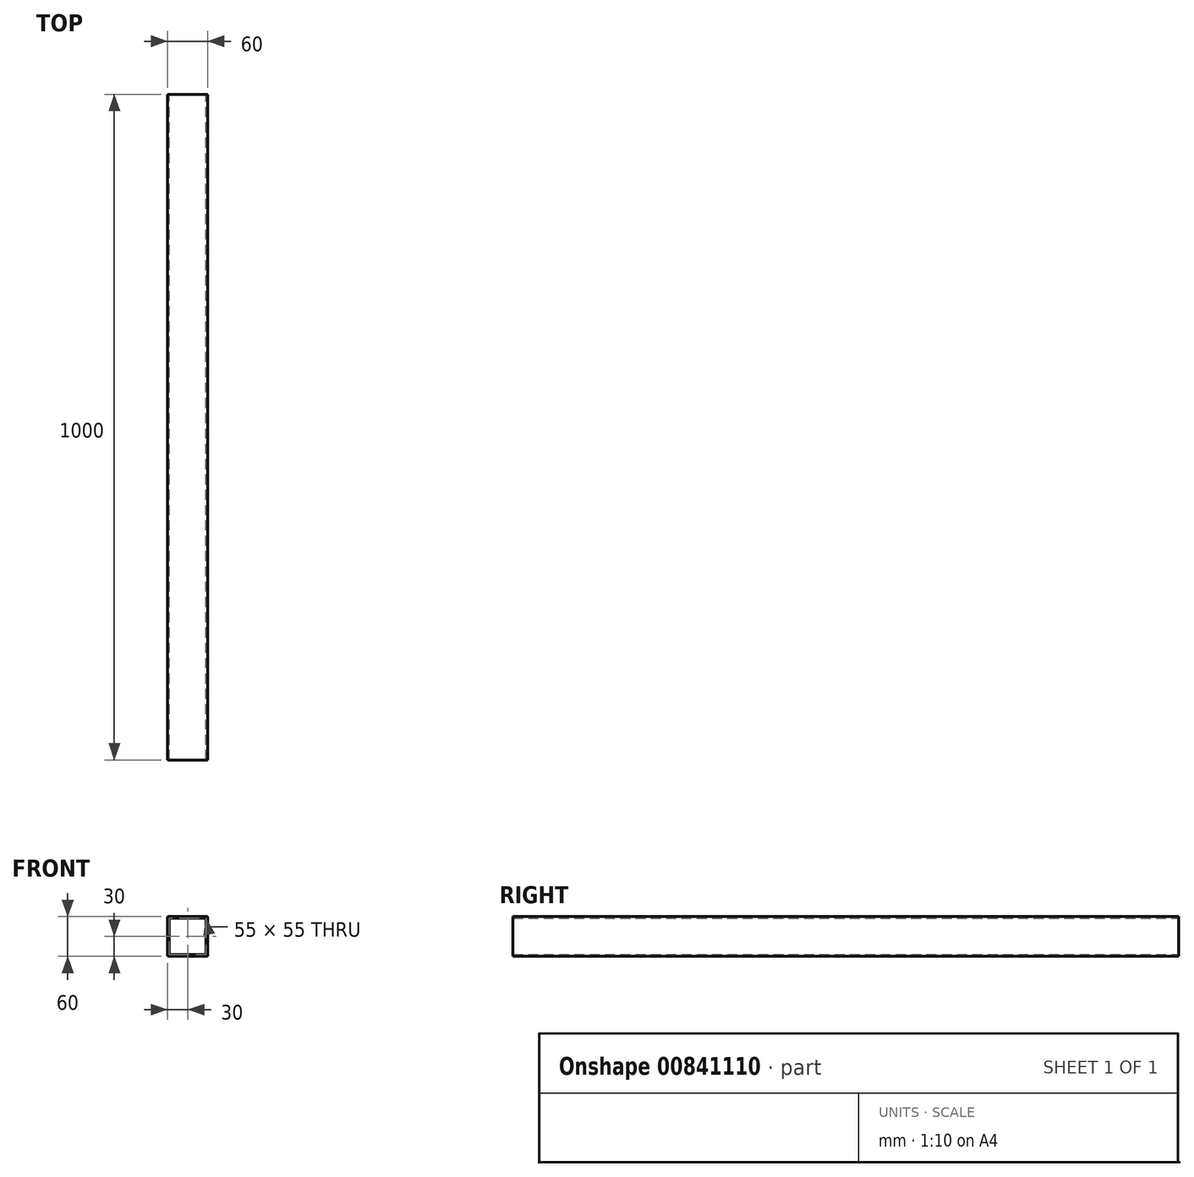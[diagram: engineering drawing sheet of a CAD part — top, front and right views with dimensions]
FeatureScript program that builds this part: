
annotation { "Feature Type Name" : "Feature", "Feature Type Description" : "" }
export const myFeature = defineFeature(function(context is Context, id is Id, definition is map)
    precondition{}
    {
        {
            var Q0;
            Q0=qCreatedBy(makeId("Front.planeOp"),FACE);
            var sketch = newSketch(context, id + "F0", { "sketchPlane" : qUnion([Q0])});
            skLineSegment(sketch, "E0.bottom", {"start": v(30, 30) * mm, "end": v(-30, 30) * mm});
            skLineSegment(sketch, "E0.top", {"start": v(30, -30) * mm, "end": v(-30, -30) * mm});
            skLineSegment(sketch, "E0.left", {"start": v(30, 30) * mm, "end": v(30, -30) * mm});
            skLineSegment(sketch, "E0.right", {"start": v(-30, 30) * mm, "end": v(-30, -30) * mm});
            skPoint(sketch, "E0.middle", {"position": v(0, 0) * mm});
            skSolve(sketch);
        }
        {
            var Q0;
            Q0=qSketchRegion(id+"F0",true);
            extrude(context, id + "F1", {"entities" : qUnion([Q0]), "depth" : 1000 * mm, "offsetDistance" : 25 * mm});
        }
        {
            var Q0;
            Q0=makeQuery(id+"F1.opExtrude","CAP_FACE",FACE,{"disambiguationData":[OSD([sQuery(id+"F0.wireOp",EDGE,"E0.bottom"),sQuery(id+"F0.wireOp",EDGE,"E0.top"),sQuery(id+"F0.wireOp",EDGE,"E0.left"),sQuery(id+"F0.wireOp",EDGE,"E0.right")])],"isStart":false});
            var Q1;
            Q1=makeQuery(id+"F1.opExtrude","CAP_FACE",FACE,{"disambiguationData":[OSD([sQuery(id+"F0.wireOp",EDGE,"E0.bottom"),sQuery(id+"F0.wireOp",EDGE,"E0.top"),sQuery(id+"F0.wireOp",EDGE,"E0.left"),sQuery(id+"F0.wireOp",EDGE,"E0.right")])],"isStart":true});
            shell(context, id + "F2", {"entities" : qUnion([Q0, Q1]), "thickness" : 2.5 * mm});
        }
    });
